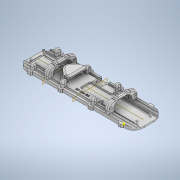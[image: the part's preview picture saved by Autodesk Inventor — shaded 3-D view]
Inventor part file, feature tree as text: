
AUTODESK INVENTOR PART (.ipt)
format: ipt  version: 2021 (Build 250183000, 183)  size: 4,560,384 bytes
history: native  units: in
note: dims shown in document units (in); Inventor stores cm internally (conversion verified against a paired STEP export)
features: fillet x19, extrude x16, sketch x16, mirror x10, plane x3, chamfer x1, revolve x1
ambient origin geometry x8: Origin, YZ Plane, XZ Plane, XY Plane, X Axis, Y Axis, Z Axis, Center Point
bodies: Solid1 (feature_tree)
feature tree (66):
  extrude  "Extrusion1"  Depth=4.9606in
  extrude  "Extrusion2"  TaperAngle=0.0deg  [1 undecoded]
  plane  "Work Plane1"
  plane  "Work Plane2"
  extrude  "Extrusion5"  Depth=0.2362in
  fillet  "Fillet2"  Radius=0.0787in
  mirror  "Mirror3"
  extrude  "Extrusion6"  TaperAngle=0.0deg  [1 undecoded]
  extrude  "Extrusion7"  Depth=0.2362in
  extrude  "Extrusion9"  [1 undecoded]
  extrude  "Extrusion10"  Depth=0.5354in
  fillet  "Fillet4"  Radius=0.9449in
  mirror  "Mirror4"
  mirror  "Mirror5"
  fillet  "Fillet5"  Radius=2.7559in
  fillet  "Fillet6"  Radius=0.4724in
  extrude  "Extrusion12"  Depth=0.0866in TaperAngle=0.0deg
  extrude  "Extrusion13"  Depth=0.0945in
  mirror  "Mirror8"
  mirror  "Mirror9"
  mirror  "Mirror10"
  fillet  "Fillet9"  Radius=0.0945in
  fillet  "Fillet11"  Radius=0.0945in
  fillet  "Fillet12"  [1 undecoded]
  extrude  "Extrusion17"  TaperAngle=0.0deg  [1 undecoded]
  fillet  "Fillet16"  [1 undecoded]
  mirror  "Mirror13"
  extrude  "Extrusion11"  Depth=1.8in
  plane  "Work Plane4"
  sketch  "Sketch52"  dims[d42=0.0in d43=0.0in d44=0.0in]
  extrude  "Extrusion24"  Depth=0.1575in TaperAngle=0.0deg
  chamfer  "Chamfer7"  Distance=0.0945in
  extrude  "Extrusion25"  Depth=0.0945in
  extrude  "Extrusion26"  Depth=0.0945in
  fillet  "Fillet32"  Radius=0.0945in
  fillet  "Fillet34"  [1 undecoded]
  mirror  "Mirror19"
  mirror  "Mirror20"
  mirror  "Mirror21"
  extrude  "Extrusion28"  TaperAngle=0.0deg  [1 undecoded]
  extrude  "Extrusion29"  TaperAngle=0.0deg  [1 undecoded]
  revolve  "Revolution10"  [1 undecoded]
  fillet  "Fillet36"  Radius=0.9in
  fillet  "Fillet37"  Radius=0.7in
  fillet  "Fillet38"  Radius=0.35in
  fillet  "Fillet39"  Radius=0.1969in
  fillet  "Fillet40"  Radius=0.4094in
  fillet  "Fillet41"  [1 undecoded]
  fillet  "Fillet42"  [1 undecoded]
  fillet  "Fillet44"  [1 undecoded]
  fillet  "Fillet45"  [1 undecoded]
  sketch  "Sketch1"  dims[d0=0.1575in d1=0.0in d2=4.9606in]
  sketch  "Sketch2"  dims[d3=1.5512in d4=0.0in]
  sketch  "Sketch7"  dims[d5=0.0in d6=0.2362in d7=0.0787in d8=0.0in]
  sketch  "Sketch8"  dims[d15=-0.7756in d16=0.0in]
  sketch  "Sketch13"  dims[d17=0.0in d18=0.2362in]
  sketch  "Sketch14"  dims[d19=1.3386in d24=-2.4803in]
  sketch  "Sketch15"  dims[d28=0.5354in d29=0.0in d30=0.5354in d31=0.9449in d32=2.7559in d33=0.4724in]
  sketch  "Sketch25"  dims[d34=0.811in d35=0.0866in d36=0.0in]
  sketch  "Sketch39"  dims[d37=0.0945in d38=0.0945in d39=0.0945in d40=0.0945in d41=0.0in]
  sketch  "Sketch53"  dims[d45=0.7in d46=1.8in]
  sketch  "Sketch54"  dims[d47=0.35in d48=0.1575in d49=0.0in]
  sketch  "Sketch55"  dims[d60=1.9685in]
  sketch  "Sketch58"  dims[d61=0.9449in]
  sketch  "Sketch59"  dims[d62=0.4724in]
  sketch  "Sketch60"  dims[d63=1.7087in d64=0.0945in d65=0.0945in d66=0.0945in d67=0.0945in d68=0.0in d69=0.0in d70=0.0in d71=0.0in d72=0.9in d73=0.7in d74=0.35in d75=0.1969in d79=0.4094in d80=0.0in d81=0.0in d82=0.0in d83=0.0in d84=0.0in d85=0.0787in d86=0.0in d88=0.3543in d89=0.315in d92=0.0394in d93=0.0in d96=1.1024in d97=0.5512in d98=0.2756in d99=0.0787in d116=0.2362in d117=0.0in d118=0.0in d119=0.1181in d120=0.0394in d121=0.0in d126=0.1339in d127=1.5748in d128=0.0in d131=0.0394in d133=0.0551in d134=0.0in d138=0.5709in d148=0.0591in d171=0.0866in d172=0.0394in d173=0.0394in d174=0.0866in d175=0.2638in d176=0.0866in d177=0.0945in d178=0.0866in d179=0.0394in d180=0.0394in d181=0.0787in d182=0.0236in d183=0.0in d184=0.0433in d204=0.0945in d263=0.8661in d264=0.4331in d278=4.7244in d279=0.0in d285=0.0in d286=0.0in d288=-1.5748in d289=0.3937in d291=0.1969in d292=0.1181in d293=0.0in d298=0.0394in d299=0.2362in d300=45.0deg d301=0.3937in d302=0.0in d303=0.1969in d304=0.0197in d305=0.1339in d306=0.0in d307=0.0in d308=0.0886in d309=0.1441in d310=0.3937in d318=0.1516in d319=0.2883in d320=0.0984in d321=0.1339in d327=0.0in d328=0.0in d329=0.0in d330=0.126in d331=0.126in d332=0.315in d333=0.7087in d334=0.3543in d335=0.3937in d336=0.0in d337=0.1772in d338=0.1969in d339=0.0in d340=0.5906in d341=180.0deg d342=0.0in d343=0.0in d348=0.0787in d349=0.0787in d350=0.0787in d351=0.0551in d352=0.0551in d353=0.0551in d354=0.0551in d356=0.0472in d357=0.0551in d146=0.0197in d147=0.0344in d149=0.0344in d211=0.0197in d212=0.0344in d213=0.0197in d214=0.0344in d287=0.0197in]
note: 14 required parameter values undecoded (feature->parameter linkage not recoverable at this tier; creation-order binding heuristic only, values carry confidence <= 0.55)